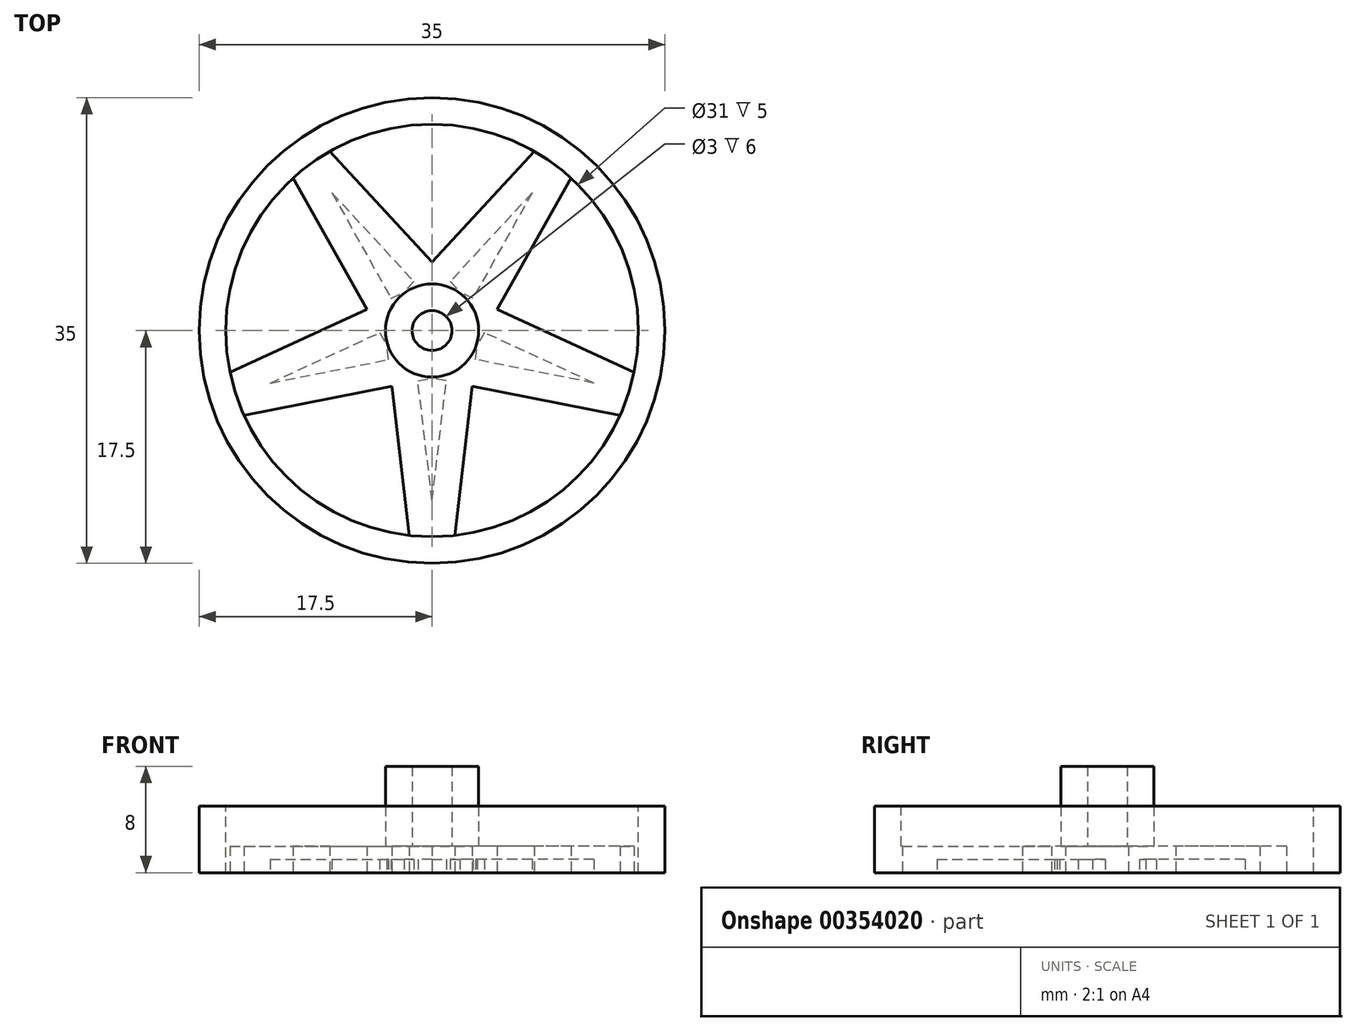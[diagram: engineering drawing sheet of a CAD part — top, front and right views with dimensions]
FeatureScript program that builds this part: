
annotation { "Feature Type Name" : "Feature", "Feature Type Description" : "" }
export const myFeature = defineFeature(function(context is Context, id is Id, definition is map)
    precondition{}
    {
        {
            var Q0;
            Q0=qCreatedBy(makeId("Top.planeOp"),FACE);
            var sketch = newSketch(context, id + "F0", { "sketchPlane" : qUnion([Q0])});
            skCircle(sketch, "E0", {"center": v(0, 0) * mm, "radius": 17.5 * mm});
            skSolve(sketch);
        }
        {
            var Q0;
            Q0=makeQuery(id+"F0.imprint","IMPRINT",FACE,{"disambiguationData":[TD([[makeQuery(id+"F0.imprint","IMPRINT",EDGE,{"derivedFrom":sQuery(id+"F0.wireOp",EDGE,"E0")}),1.0]])]});
            extrude(context, id + "F1", {"entities" : qUnion([Q0]), "depth" : 5 * mm});
        }
        {
            var Q0;
            Q0=makeQuery(id+"F1.opExtrude","CAP_FACE",FACE,{"disambiguationData":[OSD([sQuery(id+"F0.wireOp",EDGE,"E0")])],"isStart":false});
            var sketch = newSketch(context, id + "F2", { "sketchPlane" : qUnion([Q0])});
            skCircle(sketch, "E1", {"center": v(0, 0) * mm, "radius": 15.5 * mm});
            skSolve(sketch);
        }
        {
            var Q0;
            Q0=makeQuery(id+"F2.imprint","IMPRINT",FACE,{"disambiguationData":[TD([[makeQuery(id+"F2.imprint","IMPRINT",EDGE,{"derivedFrom":sQuery(id+"F2.wireOp",EDGE,"E1")}),1.0]])]});
            extrude(context, id + "F3", {"entities" : qUnion([Q0]), "operationType" : NewBodyOperationType.REMOVE, "oppositeDirection" : true, "depth" : 3 * mm});
        }
        {
            var Q0;
            Q0=makeQuery(id+"F3.boolean.opBoolean","COPY",FACE,{"derivedFrom":makeQuery(id+"F3.opExtrude","CAP_FACE",FACE,{"disambiguationData":[OSD([sQuery(id+"F2.wireOp",EDGE,"E1")])],"isStart":false})});
            var sketch = newSketch(context, id + "F4", { "sketchPlane" : qUnion([Q0])});
            skCircle(sketch, "E2", {"center": v(0, 0) * mm, "radius": 1.5 * mm});
            skCircle(sketch, "E3", {"center": v(0, 0) * mm, "radius": 3.5 * mm});
            skSolve(sketch);
        }
        {
            var Q0;
            Q0 = qSketchRegion(id + "F4", true);
            extrude(context, id + "F5", {"entities" : qUnion([Q0]), "operationType" : NewBodyOperationType.ADD, "depth" : 6 * mm});
        }
        {
            var Q0;
            Q0=makeQuery(id+"F1.opExtrude","CAP_FACE",FACE,{"disambiguationData":[OSD([sQuery(id+"F0.wireOp",EDGE,"E0")])],"isStart":true});
            var sketch = newSketch(context, id + "F6", { "sketchPlane" : qUnion([Q0])});
            skCircle(sketch, "E4", {"center": v(0, 0) * mm, "radius": 3.5 * mm});
            skCircle(sketch, "E5", {"center": v(0, 0) * mm, "radius": 15.5 * mm});
            skLineSegment(sketch, "E6", {"start": v(-1.7, 15.4) * mm, "end": v(-3.48, 0.41) * mm});
            skLineSegment(sketch, "E7.MirrorCS", {"start": v(1.7, 15.4) * mm, "end": v(3.48, 0.41) * mm});
            skLineSegment(sketch, "E8.1.0", {"start": v(-15.18, 3.14) * mm, "end": v(-1.46, -3.18) * mm});
            skLineSegment(sketch, "E8.1.1", {"start": v(-14.13, 6.38) * mm, "end": v(-3.03, 4.17) * mm});
            skLineSegment(sketch, "E8.2.0", {"start": v(-7.68, -13.47) * mm, "end": v(2.57, -2.38) * mm});
            skLineSegment(sketch, "E8.2.1", {"start": v(-10.43, -11.46) * mm, "end": v(-3.05, 1.71) * mm});
            skLineSegment(sketch, "E8.3.0", {"start": v(10.43, -11.46) * mm, "end": v(3.05, 1.71) * mm});
            skLineSegment(sketch, "E8.3.1", {"start": v(7.68, -13.47) * mm, "end": v(-2.57, -2.38) * mm});
            skLineSegment(sketch, "E8.4.0", {"start": v(14.13, 6.38) * mm, "end": v(3.03, 4.17) * mm});
            skLineSegment(sketch, "E8.4.1", {"start": v(15.18, 3.14) * mm, "end": v(1.46, -3.18) * mm});
            skLineSegment(sketch, "E9.0", {"start": v(0, 12.79) * mm, "end": v(-1.06, 3.78) * mm});
            skLineSegment(sketch, "E10.0", {"start": v(0, 12.79) * mm, "end": v(1.06, 3.78) * mm});
            skLineSegment(sketch, "E11.trimOffspring", {"start": v(1.06, 3.78) * mm, "end": v(0, 3.57) * mm});
            skPoint(sketch, "E12.orphan", {"position": v(-0.68, 3.43) * mm});
            skPoint(sketch, "E13.orphan", {"position": v(0.68, 3.43) * mm});
            skLineSegment(sketch, "E14.trimOffspring", {"start": v(-1.06, 3.78) * mm, "end": v(0, 3.57) * mm});
            skLineSegment(sketch, "E15.1.0", {"start": v(-12.16, 3.95) * mm, "end": v(-3.92, 0.16) * mm});
            skLineSegment(sketch, "E15.1.1", {"start": v(-12.16, 3.95) * mm, "end": v(-3.27, 2.18) * mm});
            skLineSegment(sketch, "E15.1.2", {"start": v(-3.27, 2.18) * mm, "end": v(-3.4, 1.1) * mm});
            skLineSegment(sketch, "E15.1.3", {"start": v(-3.92, 0.16) * mm, "end": v(-3.4, 1.1) * mm});
            skLineSegment(sketch, "E15.2.0", {"start": v(-7.52, -10.35) * mm, "end": v(-1.36, -3.68) * mm});
            skLineSegment(sketch, "E15.2.1", {"start": v(-7.52, -10.35) * mm, "end": v(-3.08, -2.43) * mm});
            skLineSegment(sketch, "E15.2.2", {"start": v(-3.08, -2.43) * mm, "end": v(-2.1, -2.89) * mm});
            skLineSegment(sketch, "E15.2.3", {"start": v(-1.36, -3.68) * mm, "end": v(-2.1, -2.89) * mm});
            skLineSegment(sketch, "E15.3.0", {"start": v(7.52, -10.35) * mm, "end": v(3.08, -2.43) * mm});
            skLineSegment(sketch, "E15.3.1", {"start": v(7.52, -10.35) * mm, "end": v(1.36, -3.68) * mm});
            skLineSegment(sketch, "E15.3.2", {"start": v(1.36, -3.68) * mm, "end": v(2.1, -2.89) * mm});
            skLineSegment(sketch, "E15.3.3", {"start": v(3.08, -2.43) * mm, "end": v(2.1, -2.89) * mm});
            skLineSegment(sketch, "E15.4.0", {"start": v(12.16, 3.95) * mm, "end": v(3.27, 2.18) * mm});
            skLineSegment(sketch, "E15.4.1", {"start": v(12.16, 3.95) * mm, "end": v(3.92, 0.16) * mm});
            skLineSegment(sketch, "E15.4.2", {"start": v(3.92, 0.16) * mm, "end": v(3.4, 1.1) * mm});
            skLineSegment(sketch, "E15.4.3", {"start": v(3.27, 2.18) * mm, "end": v(3.4, 1.1) * mm});
            skSolve(sketch);
        }
        {
            var Q0;
            Q0=makeQuery(id+"F6.imprint","IMPRINT",FACE,{"disambiguationData":[TD([[makeQuery(id+"F6.imprint","IMPRINT",EDGE,{"derivedFrom":sQuery(id+"F6.wireOp",EDGE,"E15.1.0")}),1.0]])]});
            var Q1;
            Q1=makeQuery(id+"F6.imprint","IMPRINT",FACE,{"disambiguationData":[TD([[makeQuery(id+"F6.imprint","IMPRINT",EDGE,{"derivedFrom":sQuery(id+"F6.wireOp",EDGE,"E9.0")}),1.0]])]});
            var Q2;
            Q2=makeQuery(id+"F6.imprint","IMPRINT",FACE,{"disambiguationData":[TD([[makeQuery(id+"F6.imprint","IMPRINT",EDGE,{"derivedFrom":sQuery(id+"F6.wireOp",EDGE,"E15.4.0")}),1.0]])]});
            var Q3;
            Q3=makeQuery(id+"F6.imprint","IMPRINT",FACE,{"disambiguationData":[TD([[makeQuery(id+"F6.imprint","IMPRINT",EDGE,{"derivedFrom":sQuery(id+"F6.wireOp",EDGE,"E15.3.0")}),1.0]])]});
            var Q4;
            Q4=makeQuery(id+"F6.imprint","IMPRINT",FACE,{"disambiguationData":[TD([[makeQuery(id+"F6.imprint","IMPRINT",EDGE,{"derivedFrom":sQuery(id+"F6.wireOp",EDGE,"E15.2.0")}),1.0]])]});
            extrude(context, id + "F7", {"entities" : qUnion([Q0, Q1, Q2, Q3, Q4]), "operationType" : NewBodyOperationType.REMOVE, "oppositeDirection" : true, "depth" : 1 * mm});
        }
        {
            var Q0;
            {var subQ0=sQuery(id+"F6.wireOp",EDGE,"E8.2.0");var subQ1=sQuery(id+"F6.wireOp",EDGE,"E5");var subQ2=makeQuery(id+"F6.imprint","INTERSECT",VERTEX,{"derivedFrom":[subQ1,subQ0]});Q0=makeQuery(id+"F6.imprint","IMPRINT",FACE,{"disambiguationData":[TD([[makeQuery(id+"F6.imprint","IMPRINT",EDGE,{"disambiguationData":[TD([[subQ2,-1.0]])],"derivedFrom":subQ1}),1.0]])]});}
            var Q1;
            {var subQ0=sQuery(id+"F6.wireOp",EDGE,"E8.1.0");var subQ1=sQuery(id+"F6.wireOp",EDGE,"E5");var subQ2=makeQuery(id+"F6.imprint","INTERSECT",VERTEX,{"derivedFrom":[subQ1,subQ0]});Q1=makeQuery(id+"F6.imprint","IMPRINT",FACE,{"disambiguationData":[TD([[makeQuery(id+"F6.imprint","IMPRINT",EDGE,{"disambiguationData":[TD([[subQ2,-1.0]])],"derivedFrom":subQ1}),1.0]])]});}
            var Q2;
            {var subQ3=sQuery(id+"F6.wireOp",EDGE,"E8.4.0");Q2=makeQuery(id+"F6.imprint","IMPRINT",FACE,{"disambiguationData":[TD([[makeQuery(id+"F6.imprint","IMPRINT",EDGE,{"derivedFrom":subQ3}),-1.0]])]});}
            var Q3;
            {var subQ0=sQuery(id+"F6.wireOp",EDGE,"E8.3.0");var subQ1=sQuery(id+"F6.wireOp",EDGE,"E5");var subQ2=makeQuery(id+"F6.imprint","INTERSECT",VERTEX,{"derivedFrom":[subQ1,subQ0]});Q3=makeQuery(id+"F6.imprint","IMPRINT",FACE,{"disambiguationData":[TD([[makeQuery(id+"F6.imprint","IMPRINT",EDGE,{"disambiguationData":[TD([[subQ2,-1.0]])],"derivedFrom":subQ1}),1.0]])]});}
            var Q4;
            {var subQ3=sQuery(id+"F6.wireOp",EDGE,"E8.1.1");Q4=makeQuery(id+"F6.imprint","IMPRINT",FACE,{"disambiguationData":[TD([[makeQuery(id+"F6.imprint","IMPRINT",EDGE,{"derivedFrom":subQ3}),1.0]])]});}
            extrude(context, id + "F8", {"entities" : qUnion([Q0, Q1, Q2, Q3, Q4]), "operationType" : NewBodyOperationType.REMOVE, "oppositeDirection" : true, "depth" : 2 * mm});
        }
    });
